# Revit family: NBS_ConceptCubicleSystems_VntyUnits_LaminateVanityUnits
name_source: partatom
category: Casework
units: mm (PartAtom-declared; Revit-internal decimal feet)

## family parameters
Always vertical = Yes
Cut with Voids When Loaded = No
Room Calculation Point = No
Shared = No
Work Plane-Based = No

## types (2) — shared parameters
AccessPanelHeight = 450 mm  [stored 1.47638 ft]
AccessPanelThickness = 13 mm  [stored 0.0426509 ft]
AccesssPanelMaterial = NBS_ConceptCubicleSystems_CompactGradeLaminate
Application = Suitable for inset or semi-recessed sinks
AssetType = Fixed
CabinetMaterial = NBS_ConceptCubicleSystems_CompactGradeLaminate
Category = Pr_40_20_76_94:Vanity units
Color = Colours can match or contrast our cubicles and duct sets to create a uniform washroom
CounterTopHeight = 800 mm  [stored 2.62467 ft]
CounterTopMaterial = NBS_ConceptCubicleSystems_HighPressureLaminatedMR
CounterTopThickness = 19 mm  [stored 0.062336 ft]
Description = Laminate vanity units
DownstandHeight = 200 mm  [stored 0.656168 ft]
DurationUnit = year
Features = Suitable for inset or semi-recessed sinks, Hook on or push on clips (standard) or hinged and lockable if used for storage, 350 mm for semi-recessed WHBs or 600 mm deep for inset WHBs
FrameworkThickness = 13 mm  [stored 0.0426509 ft]
Height = 800 mm  [stored 2.62467 ft]
HeightOptions = 600 mm, 650 mm, 700 mm
IfcExportAs = IfcFurnitureType
IfcExportType = USERDEFINED
IsBuiltIn = Yes
ManufacturerName = Concept Cubicle Systems
ManufacturerURL = www.conceptcubiclesystems.co.uk
Material = Material choice based on environment
ModelReference = Laminate Vanity Units
NBSCertification = www.nationalbimlibrary.com/cert/00e2clc1
NBSDescription = Vanity units
NBSReference = 45-35-72/378
NominalHeight = 800 mm  [stored 2.62467 ft]
ProductInformation = https://www.conceptcubiclesystems.co.uk
Status = UNSET
Style = Vanity units
SystemManufacturer = Concept Cubicle Systems
Uniclass2015Code = Pr_40_20_76_94
Uniclass2015Title = Vanity units
Uniclass2015Version = Products v1.17
UpstandHeight = 100 mm  [stored 0.328084 ft]
Version = 1
WarrantyDurationUnit = year
zero-valued in all types: Default Elevation

## per-type parameters (varying)
| type | BIMObjectName | CounterTopDepth | Depth | Name | NominalDepth |
| CounterTopVanity | NBS_ConceptCubicleSystems_VanityUnits_LaminateVanityUnits_CounterTopVanity | 600 mm | 600 mm | VanityUnits_LaminateVanityUnits_CounterTopVanity_ConceptCubicleSystems | 600 mm |
| SemiRecessedVanity | NBS_ConceptCubicleSystems_VanityUnits_LaminateVanityUnits_SemiRecessedVanity | 350 mm | 350 mm | VanityUnits_LaminateVanityUnits_SemiRecessedVanity_ConceptCubicleSystems | 350 mm |

note: [stored X ft] marks values corroborated as IEEE doubles in the binary element streams (Revit-internal decimal feet)

## geometry (parser evidence)
native form markers: Sweep x4
no freeform markers — native parametric forms only
